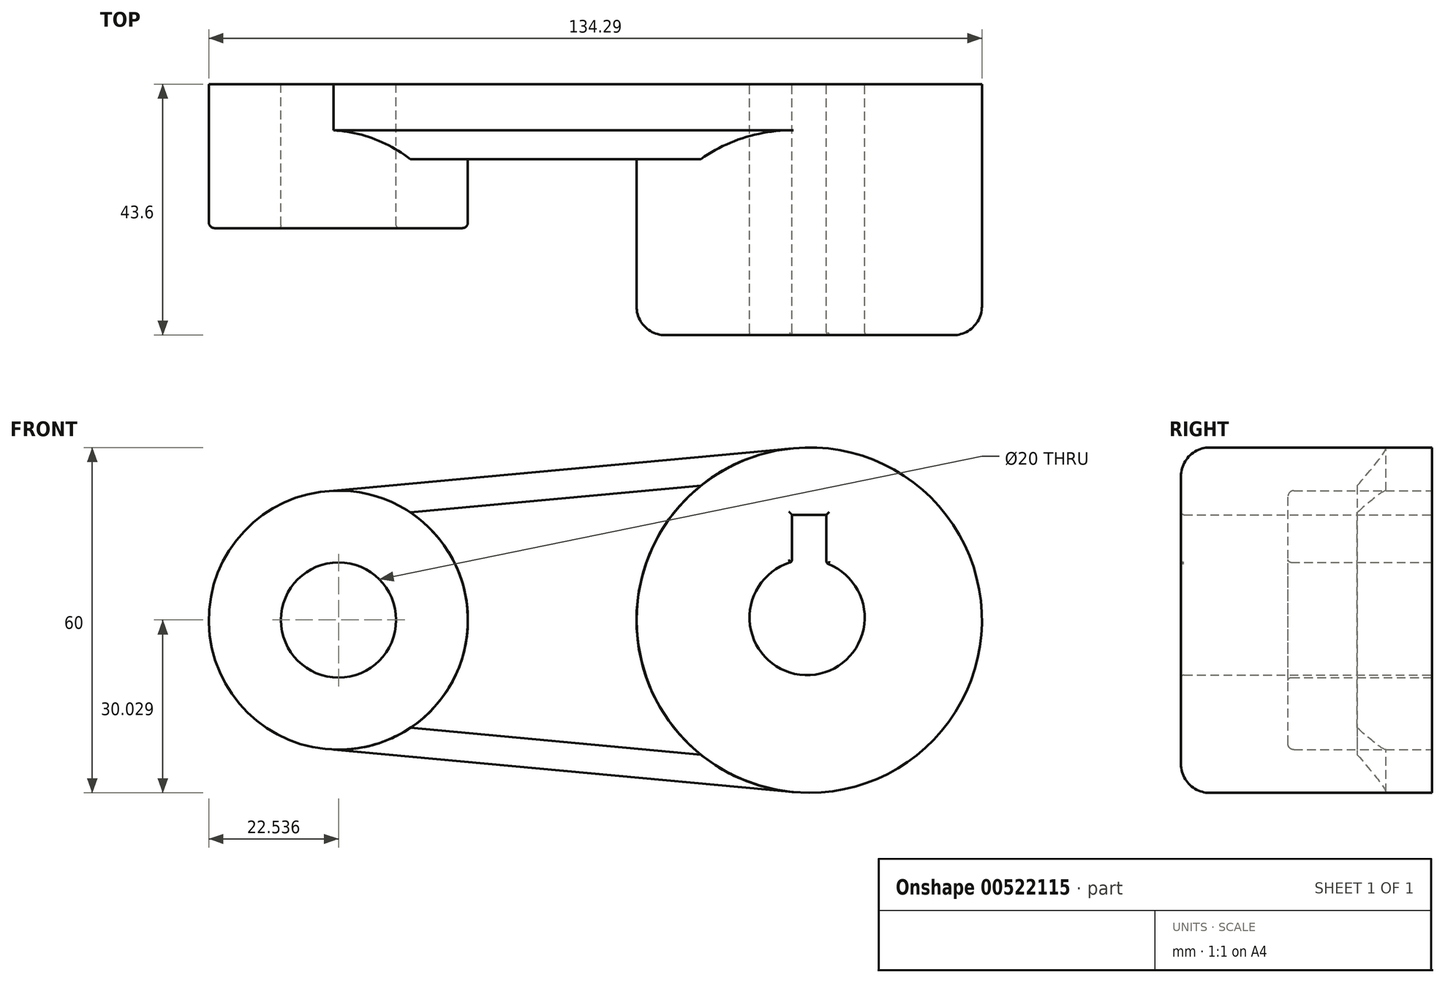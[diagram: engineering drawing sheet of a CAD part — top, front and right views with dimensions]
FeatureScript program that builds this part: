
annotation { "Feature Type Name" : "Feature", "Feature Type Description" : "" }
export const myFeature = defineFeature(function(context is Context, id is Id, definition is map)
    precondition{}
    {
        {
            var Q0;
            Q0=qCreatedBy(makeId("Front.planeOp"),FACE);
            var sketch = newSketch(context, id + "F0", { "sketchPlane" : qUnion([Q0])});
            skCircle(sketch, "E0", {"center": v(0, 0) * mm, "radius": 30 * mm});
            skCircle(sketch, "E1", {"center": v(-81.79, 0) * mm, "radius": 22.5 * mm});
            skCircle(sketch, "E2", {"center": v(-81.75, 0.03) * mm, "radius": 10 * mm});
            skCircle(sketch, "E3", {"center": v(-0.37, 0.45) * mm, "radius": 10 * mm});
            skLineSegment(sketch, "E4.bottom", {"start": v(3, 18.3) * mm, "end": v(-3, 18.3) * mm});
            skLineSegment(sketch, "E4.top", {"start": v(3, -6.7) * mm, "end": v(-3, -6.7) * mm});
            skLineSegment(sketch, "E4.left", {"start": v(3, 18.3) * mm, "end": v(3, -6.7) * mm});
            skLineSegment(sketch, "E4.right", {"start": v(-3, 18.3) * mm, "end": v(-3, -6.7) * mm});
            skPoint(sketch, "E4.middle", {"position": v(0, 5.8) * mm});
            skLineSegment(sketch, "E5", {"start": v(-82.65, 22.48) * mm, "end": v(0, 30.13) * mm});
            skLineSegment(sketch, "E6", {"start": v(-82.65, -22.48) * mm, "end": v(0, -30.13) * mm});
            skSolve(sketch);
        }
        {
            var Q0;
            Q0=makeQuery(id+"F0.imprint","IMPRINT",FACE,{"disambiguationData":[TD([[makeQuery(id+"F0.imprint","IMPRINT",EDGE,{"derivedFrom":sQuery(id+"F0.wireOp",EDGE,"E2")}),-1.0]])]});
            extrude(context, id + "F1", {"entities" : qUnion([Q0]), "depth" : 25 * mm, "offsetDistance" : 25 * mm});
        }
        {
            var Q0;
            {var subQ0=sQuery(id+"F0.wireOp",EDGE,"E5");var subQ1=sQuery(id+"F0.wireOp",EDGE,"E0");var subQ2=makeQuery(id+"F0.imprint","INTERSECT",VERTEX,{"derivedFrom":[subQ1,subQ0]});Q0=makeQuery(id+"F0.imprint","IMPRINT",FACE,{"disambiguationData":[TD([[makeQuery(id+"F0.imprint","IMPRINT",EDGE,{"disambiguationData":[TD([[subQ2,-1.0]])],"derivedFrom":subQ1}),-1.0]])]});}
            extrude(context, id + "F2", {"entities" : qUnion([Q0]), "operationType" : NewBodyOperationType.ADD, "depth" : 13 * mm, "offsetDistance" : 25 * mm});
        }
        {
            var Q0;
            {var subQ0=sQuery(id+"F0.wireOp",EDGE,"E4.bottom");Q0=makeQuery(id+"F0.imprint","IMPRINT",FACE,{"disambiguationData":[TD([[makeQuery(id+"F0.imprint","IMPRINT",EDGE,{"derivedFrom":subQ0}),-1.0]])]});}
            extrude(context, id + "F3", {"entities" : qUnion([Q0]), "operationType" : NewBodyOperationType.ADD, "depth" : 43.6 * mm, "offsetDistance" : 25 * mm});
        }
        {
            var Q0;
            Q0=makeQuery(id+"F1.opExtrude","CAP_EDGE",EDGE,{"disambiguationData":[OSD([sQuery(id+"F0.wireOp",EDGE,"E1")])],"isStart":false});
            fillet(context, id + "F4", {"entities" : qUnion([Q0]), "radius" : 1 * mm, "tangentPropagation" : true, "allowEdgeOverflow" : false});
        }
        {
            var Q0;
            Q0=makeQuery(id+"F3.opExtrude","CAP_EDGE",EDGE,{"disambiguationData":[OSD([sQuery(id+"F0.wireOp",EDGE,"E0")])],"isStart":false});
            fillet(context, id + "F5", {"entities" : qUnion([Q0]), "radius" : 5 * mm, "tangentPropagation" : true, "allowEdgeOverflow" : false});
        }
        {
            var Q0;
            Q0=makeQuery(id+"F1.opExtrude","CAP_EDGE",EDGE,{"disambiguationData":[OSD([sQuery(id+"F0.wireOp",EDGE,"E2")])],"isStart":false});
            fillet(context, id + "F6", {"entities" : qUnion([Q0]), "radius" : 0.5 * mm, "tangentPropagation" : true, "allowEdgeOverflow" : false});
        }
        {
            var Q0;
            Q0=makeQuery(id+"F3.opExtrude","CAP_EDGE",EDGE,{"disambiguationData":[OSD([sQuery(id+"F0.wireOp",EDGE,"E3")])],"isStart":false});
            fillet(context, id + "F7", {"entities" : qUnion([Q0]), "radius" : 0.5 * mm, "tangentPropagation" : true, "allowEdgeOverflow" : false});
        }
        {
            var Q0;
            Q0=makeQuery(id+"F3.opExtrude","CAP_EDGE",EDGE,{"disambiguationData":[OSD([sQuery(id+"F0.wireOp",EDGE,"E4.right")])],"isStart":false});
            fillet(context, id + "F8", {"entities" : qUnion([Q0]), "radius" : 0.5 * mm, "tangentPropagation" : true, "allowEdgeOverflow" : false});
        }
        {
            var Q0;
            Q0=makeQuery(id+"F3.opExtrude","CAP_EDGE",EDGE,{"disambiguationData":[OSD([sQuery(id+"F0.wireOp",EDGE,"E4.bottom")])],"isStart":false});
            fillet(context, id + "F9", {"entities" : qUnion([Q0]), "radius" : 0.5 * mm, "tangentPropagation" : true, "allowEdgeOverflow" : false});
        }
        {
            var Q0;
            Q0=makeQuery(id+"F3.opExtrude","CAP_EDGE",EDGE,{"disambiguationData":[OSD([sQuery(id+"F0.wireOp",EDGE,"E4.left")])],"isStart":false});
            fillet(context, id + "F10", {"entities" : qUnion([Q0]), "radius" : 0.5 * mm, "tangentPropagation" : true, "allowEdgeOverflow" : false});
        }
        {
            var Q0;
            Q0=makeQuery(id+"F2.opExtrude","CAP_EDGE",EDGE,{"disambiguationData":[OSD([sQuery(id+"F0.wireOp",EDGE,"E6")])],"isStart":false});
            chamfer(context, id + "F11", {"entities" : qUnion([Q0]), "width" : 5 * mm, "tangentPropagation" : true});
        }
        {
            var Q0;
            Q0=makeQuery(id+"F2.opExtrude","CAP_EDGE",EDGE,{"disambiguationData":[OSD([sQuery(id+"F0.wireOp",EDGE,"E5")])],"isStart":false});
            chamfer(context, id + "F12", {"entities" : qUnion([Q0]), "width" : 5 * mm, "tangentPropagation" : true});
        }
    });
